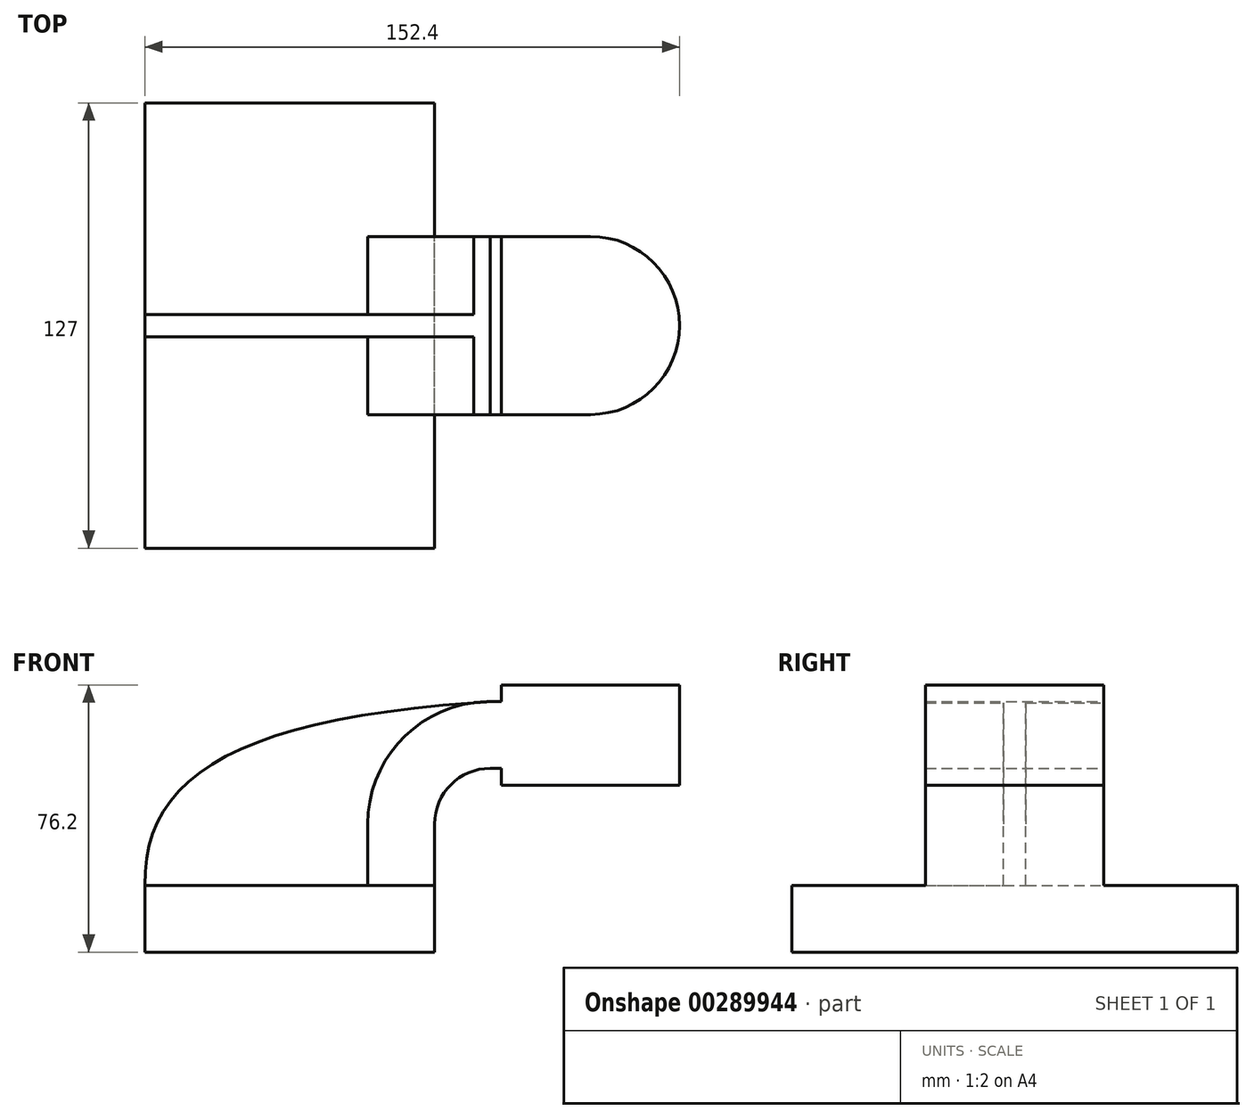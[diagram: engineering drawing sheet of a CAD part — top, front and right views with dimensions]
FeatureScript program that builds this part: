
annotation { "Feature Type Name" : "Feature", "Feature Type Description" : "" }
export const myFeature = defineFeature(function(context is Context, id is Id, definition is map)
    precondition{}
    {
        {
            var Q0;
            Q0=qCreatedBy(makeId("Front.planeOp"),FACE);
            var sketch = newSketch(context, id + "F0", { "sketchPlane" : qUnion([Q0])});
            skLineSegment(sketch, "E0.bottom", {"start": v(41.28, -9.52) * mm, "end": v(-41.28, -9.53) * mm});
            skLineSegment(sketch, "E0.top", {"start": v(41.28, 9.53) * mm, "end": v(-41.28, 9.53) * mm});
            skLineSegment(sketch, "E0.left", {"start": v(41.28, -9.52) * mm, "end": v(41.28, 9.53) * mm});
            skLineSegment(sketch, "E0.right", {"start": v(-41.28, -9.53) * mm, "end": v(-41.28, 9.52) * mm});
            skPoint(sketch, "E0.middle", {"position": v(0, 0) * mm});
            skLineSegment(sketch, "E1.bottom", {"start": v(111.12, 38.1) * mm, "end": v(60.33, 38.1) * mm});
            skLineSegment(sketch, "E1.top", {"start": v(111.12, 66.68) * mm, "end": v(60.33, 66.68) * mm});
            skLineSegment(sketch, "E1.left", {"start": v(111.12, 38.1) * mm, "end": v(111.12, 66.68) * mm});
            skLineSegment(sketch, "E1.right", {"start": v(60.33, 38.1) * mm, "end": v(60.33, 66.68) * mm});
            skPoint(sketch, "E1.middle", {"position": v(85.72, 52.39) * mm});
            skLineSegment(sketch, "E2", {"start": v(41.28, 9.53) * mm, "end": v(41.28, 27) * mm});
            skArc(sketch, "E3", {"start": v(41.28, 27) * mm, "mid": v(45.92, 38.23) * mm, "end": v(57.15, 42.88) * mm});
            skLineSegment(sketch, "E4", {"start": v(57.15, 42.88) * mm, "end": v(85.73, 42.88) * mm});
            skLineSegment(sketch, "E5.0", {"start": v(57.15, 61.93) * mm, "end": v(85.73, 61.93) * mm});
            skArc(sketch, "E5.1", {"start": v(22.23, 27) * mm, "mid": v(32.45, 51.7) * mm, "end": v(57.15, 61.93) * mm});
            skLineSegment(sketch, "E5.2", {"start": v(22.23, 9.53) * mm, "end": v(22.23, 27) * mm});
            skLineSegment(sketch, "E6", {"start": v(85.72, 38.1) * mm, "end": v(85.72, 66.68) * mm});
            skFitSpline(sketch, "E7", {"points": [v(-41.28, 9.52) * mm, v(57.15, 61.93) * mm], "startDerivative": vector(-1.7, 93.73) * mm, "endDerivative": vector(215.6, 13.75) * mm});
            skSolve(sketch);
        }
        {
            var Q0;
            Q0=makeQuery(id+"F0.imprint","IMPRINT",FACE,{"disambiguationData":[TD([[makeQuery(id+"F0.imprint","IMPRINT",EDGE,{"derivedFrom":sQuery(id+"F0.wireOp",EDGE,"E0.bottom")}),-1.0]])]});
            extrude(context, id + "F1", {"entities" : qUnion([Q0]), "endBound" : BoundingType.SYMMETRIC, "depth" : 127 * mm});
        }
        {
            var Q0;
            {var subQ1=sQuery(id+"F0.wireOp",EDGE,"E2");Q0=makeQuery(id+"F0.imprint","IMPRINT",FACE,{"disambiguationData":[TD([[makeQuery(id+"F0.imprint","IMPRINT",EDGE,{"derivedFrom":subQ1}),1.0]])]});}
            var Q1;
            {var subQ0=sQuery(id+"F0.wireOp",EDGE,"E4");var subQ1=sQuery(id+"F0.wireOp",EDGE,"E1.right");var subQ2=makeQuery(id+"F0.imprint","INTERSECT",VERTEX,{"derivedFrom":[subQ1,subQ0]});Q1=makeQuery(id+"F0.imprint","IMPRINT",FACE,{"disambiguationData":[TD([[makeQuery(id+"F0.imprint","IMPRINT",EDGE,{"disambiguationData":[TD([[subQ2,-1.0]])],"derivedFrom":subQ1}),-1.0]])]});}
            var Q2;
            {var subQ0=sQuery(id+"F0.wireOp",EDGE,"E1.right");var subQ1=sQuery(id+"F0.wireOp",EDGE,"E1.top");var subQ2=makeQuery(id+"F0.imprint","INTERSECT",VERTEX,{"derivedFrom":[subQ1,subQ0]});Q2=makeQuery(id+"F0.imprint","IMPRINT",FACE,{"disambiguationData":[TD([[makeQuery(id+"F0.imprint","IMPRINT",EDGE,{"disambiguationData":[TD([[subQ2,1.0]])],"derivedFrom":subQ1}),1.0]])]});}
            var Q3;
            {var subQ0=sQuery(id+"F0.wireOp",EDGE,"E1.right");var subQ1=sQuery(id+"F0.wireOp",EDGE,"E1.bottom");var subQ2=makeQuery(id+"F0.imprint","INTERSECT",VERTEX,{"derivedFrom":[subQ1,subQ0]});Q3=makeQuery(id+"F0.imprint","IMPRINT",FACE,{"disambiguationData":[TD([[makeQuery(id+"F0.imprint","IMPRINT",EDGE,{"disambiguationData":[TD([[subQ2,1.0]])],"derivedFrom":subQ1}),-1.0]])]});}
            extrude(context, id + "F2", {"entities" : qUnion([Q0, Q1, Q2, Q3]), "operationType" : NewBodyOperationType.ADD, "endBound" : BoundingType.SYMMETRIC, "depth" : 50.8 * mm});
        }
        {
            var Q0;
            {var subQ3=sQuery(id+"F0.wireOp",EDGE,"E5.2");Q0=makeQuery(id+"F0.imprint","IMPRINT",FACE,{"disambiguationData":[TD([[makeQuery(id+"F0.imprint","IMPRINT",EDGE,{"derivedFrom":subQ3}),1.0]])]});}
            extrude(context, id + "F3", {"entities" : qUnion([Q0]), "operationType" : NewBodyOperationType.ADD, "endBound" : BoundingType.SYMMETRIC, "depth" : 6.35 * mm});
        }
        {
            var Q0;
            {var subQ0=sQuery(id+"F0.wireOp",EDGE,"E1.left");Q0=makeQuery(id+"F0.imprint","IMPRINT",FACE,{"disambiguationData":[TD([[makeQuery(id+"F0.imprint","IMPRINT",EDGE,{"derivedFrom":subQ0}),1.0]])]});}
            var Q1;
            Q1=sQuery(id+"F0.wireOp",EDGE,"E6");
            revolve(context, id + "F4", {"operationType" : NewBodyOperationType.ADD, "entities" : qUnion([Q0]), "axis" : qUnion([Q1]), "revolveType" : RevolveType.FULL});
        }
    });
